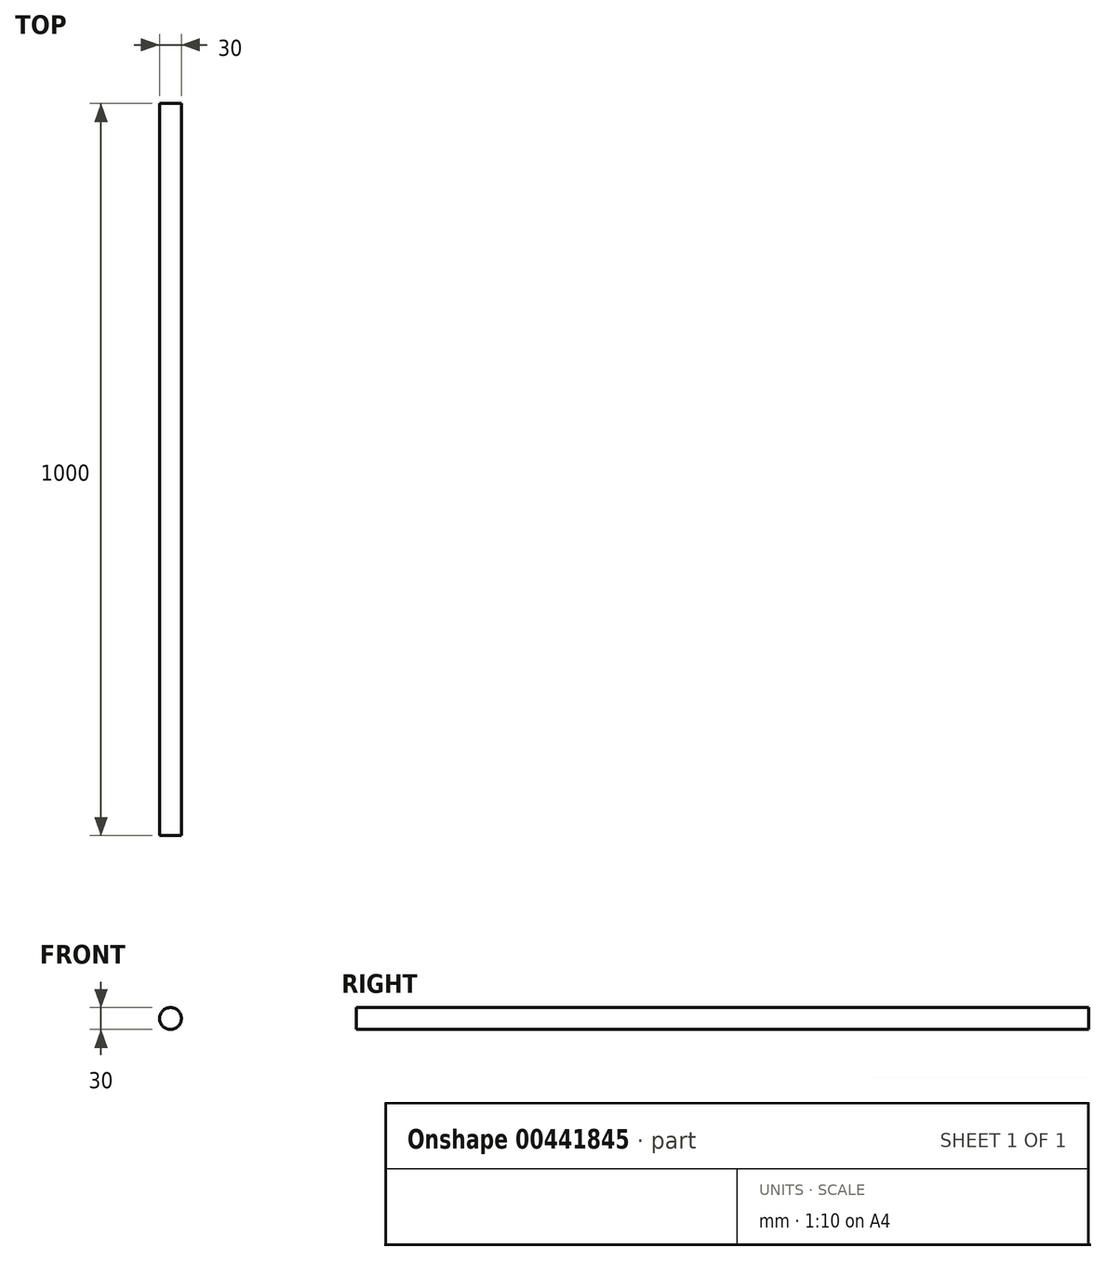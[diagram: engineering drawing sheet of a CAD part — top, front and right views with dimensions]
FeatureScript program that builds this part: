
annotation { "Feature Type Name" : "Feature", "Feature Type Description" : "" }
export const myFeature = defineFeature(function(context is Context, id is Id, definition is map)
    precondition{}
    {
        {
            var Q0;
            Q0=qCreatedBy(makeId("Front.planeOp"),FACE);
            var sketch = newSketch(context, id + "F0", { "sketchPlane" : qUnion([Q0])});
            skCircle(sketch, "E0", {"center": v(0, 0) * mm, "radius": 15 * mm});
            skSolve(sketch);
        }
        {
            var Q0;
            Q0=makeQuery(id+"F0.imprint","IMPRINT",FACE,{"disambiguationData":[TD([[makeQuery(id+"F0.imprint","IMPRINT",EDGE,{"derivedFrom":sQuery(id+"F0.wireOp",EDGE,"E0")}),1.0]])]});
            extrude(context, id + "F1", {"entities" : qUnion([Q0]), "depth" : 1000 * mm});
        }
    });
